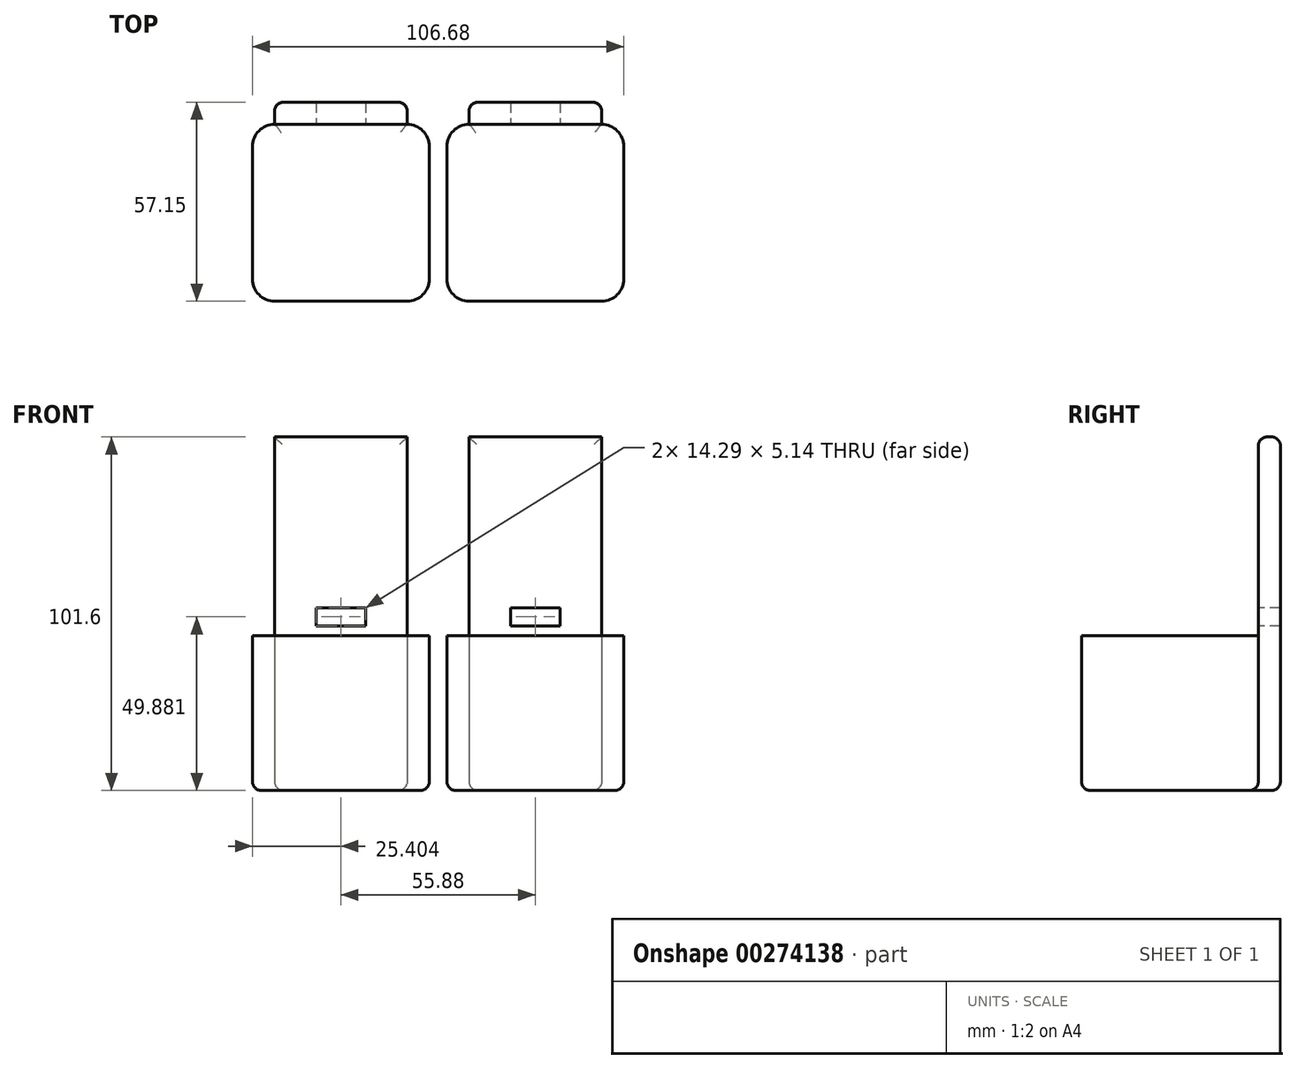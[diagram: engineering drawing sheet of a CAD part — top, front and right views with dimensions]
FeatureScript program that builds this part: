
annotation { "Feature Type Name" : "Feature", "Feature Type Description" : "" }
export const myFeature = defineFeature(function(context is Context, id is Id, definition is map)
    precondition{}
    {
        {
            var Q0;
            Q0=qCreatedBy(makeId("Top.planeOp"),FACE);
            var sketch = newSketch(context, id + "F0", { "sketchPlane" : qUnion([Q0])});
            skLineSegment(sketch, "E0.bottom", {"start": v(-13.8, 18.6) * mm, "end": v(24.3, 18.6) * mm});
            skLineSegment(sketch, "E0.top", {"start": v(-13.8, -32.2) * mm, "end": v(24.3, -32.2) * mm});
            skLineSegment(sketch, "E0.left", {"start": v(-20.15, 12.26) * mm, "end": v(-20.15, -25.84) * mm});
            skLineSegment(sketch, "E0.right", {"start": v(30.65, 12.26) * mm, "end": v(30.65, -25.84) * mm});
            skPoint(sketch, "E1.visualSharp", {"position": v(-20.15, 18.6) * mm});
            skArc(sketch, "E1.filletArc", {"start": v(-13.8, 18.6) * mm, "mid": v(-18.29, 16.75) * mm, "end": v(-20.15, 12.26) * mm});
            skPoint(sketch, "E2.visualSharp", {"position": v(30.65, 18.6) * mm});
            skArc(sketch, "E2.filletArc", {"start": v(30.65, 12.26) * mm, "mid": v(28.8, 16.75) * mm, "end": v(24.3, 18.6) * mm});
            skPoint(sketch, "E3.visualSharp", {"position": v(30.65, -32.2) * mm});
            skArc(sketch, "E3.filletArc", {"start": v(24.3, -32.2) * mm, "mid": v(28.8, -30.33) * mm, "end": v(30.65, -25.84) * mm});
            skPoint(sketch, "E4.visualSharp", {"position": v(-20.15, -32.2) * mm});
            skArc(sketch, "E4.filletArc", {"start": v(-20.15, -25.84) * mm, "mid": v(-18.29, -30.33) * mm, "end": v(-13.8, -32.2) * mm});
            skSolve(sketch);
        }
        {
            var Q0;
            Q0 = qSketchRegion(id + "F0", true);
            var Q1;
            Q1 = qSketchRegion(id + "F2", true);
            extrude(context, id + "F1", {"entities" : qUnion([Q0, Q1]), "depth" : 44.45 * mm});
        }
        {
            var Q0;
            Q0=makeQuery(id+"F1.opExtrude","SWEPT_FACE",FACE,{"disambiguationData":[OSD([sQuery(id+"F0.wireOp",EDGE,"E0.bottom")])]});
            var sketch = newSketch(context, id + "F2", { "sketchPlane" : qUnion([Q0])});
            skLineSegment(sketch, "E5.bottom", {"start": v(-24.3, 0) * mm, "end": v(13.8, 0) * mm});
            skLineSegment(sketch, "E5.top", {"start": v(-24.3, 101.6) * mm, "end": v(13.8, 101.6) * mm});
            skLineSegment(sketch, "E5.left", {"start": v(-24.3, 0) * mm, "end": v(-24.3, 101.6) * mm});
            skLineSegment(sketch, "E5.right", {"start": v(13.8, 0) * mm, "end": v(13.8, 101.6) * mm});
            skLineSegment(sketch, "E6.bottom", {"start": v(-12.4, 47.31) * mm, "end": v(1.89, 47.31) * mm});
            skLineSegment(sketch, "E6.top", {"start": v(-12.4, 52.45) * mm, "end": v(1.89, 52.45) * mm});
            skLineSegment(sketch, "E6.left", {"start": v(-12.4, 47.31) * mm, "end": v(-12.4, 52.45) * mm});
            skLineSegment(sketch, "E6.right", {"start": v(1.89, 47.31) * mm, "end": v(1.89, 52.45) * mm});
            skSolve(sketch);
        }
        {
            var Q0;
            {var subQ0=sQuery(id+"F2.wireOp",EDGE,"E5.bottom");Q0=makeQuery(id+"F2.imprint","IMPRINT",FACE,{"disambiguationData":[TD([[makeQuery(id+"F2.imprint","IMPRINT",EDGE,{"derivedFrom":subQ0}),-1.0]])]});}
            var Q1;
            {var subQ2=sQuery(id+"F2.wireOp",EDGE,"E5.top");Q1=makeQuery(id+"F2.imprint","IMPRINT",FACE,{"disambiguationData":[TD([[makeQuery(id+"F2.imprint","IMPRINT",EDGE,{"derivedFrom":subQ2}),-1.0]])]});}
            extrude(context, id + "F3", {"entities" : qUnion([Q0, Q1]), "operationType" : NewBodyOperationType.ADD, "depth" : 6.35 * mm});
        }
        {
            var Q0;
            Q0=makeQuery(id+"F1.opExtrude","SWEPT_BODY",BODY,{"disambiguationData":[OSD([sQuery(id+"F0.wireOp",EDGE,"E0.bottom"),sQuery(id+"F0.wireOp",EDGE,"E0.top"),sQuery(id+"F0.wireOp",EDGE,"E0.left"),sQuery(id+"F0.wireOp",EDGE,"E0.right"),sQuery(id+"F0.wireOp",EDGE,"E1.filletArc"),sQuery(id+"F0.wireOp",EDGE,"E2.filletArc"),sQuery(id+"F0.wireOp",EDGE,"E3.filletArc"),sQuery(id+"F0.wireOp",EDGE,"E4.filletArc")])]});
            transform(context, id + "F4", {"entities" : qUnion([Q0]), "transformType" : TransformType.TRANSLATION_3D, "dx" : 55.88 * mm, "dy" : 0 * mm, "dz" : 0 * mm, "makeCopy" : true});
        }
        {
            var Q0;
            Q0=makeQuery(id+"F4.opPattern","COPY",EDGE,{"derivedFrom":makeQuery(id+"F3.opExtrude","CAP_EDGE",EDGE,{"disambiguationData":[OSD([sQuery(id+"F2.wireOp",EDGE,"E5.left")])],"isStart":false}),"instanceName":"1"});
            var Q1;
            Q1=makeQuery(id+"F3.opExtrude","CAP_EDGE",EDGE,{"disambiguationData":[OSD([sQuery(id+"F2.wireOp",EDGE,"E5.left")])],"isStart":false});
            var Q2;
            Q2=makeQuery(id+"F3.opExtrude","CAP_EDGE",EDGE,{"disambiguationData":[OSD([sQuery(id+"F2.wireOp",EDGE,"E5.right")])],"isStart":false});
            var Q3;
            Q3=makeQuery(id+"F4.opPattern","COPY",EDGE,{"derivedFrom":makeQuery(id+"F3.opExtrude","CAP_EDGE",EDGE,{"disambiguationData":[OSD([sQuery(id+"F2.wireOp",EDGE,"E5.right")])],"isStart":false}),"instanceName":"1"});
            var Q4;
            Q4=makeQuery(id+"F3.opExtrude","CAP_EDGE",EDGE,{"disambiguationData":[OSD([sQuery(id+"F2.wireOp",EDGE,"E5.top")])],"isStart":false});
            var Q5;
            Q5=makeQuery(id+"F4.opPattern","COPY",EDGE,{"derivedFrom":makeQuery(id+"F3.opExtrude","CAP_EDGE",EDGE,{"disambiguationData":[OSD([sQuery(id+"F2.wireOp",EDGE,"E5.top")])],"isStart":false}),"instanceName":"1"});
            var Q6;
            Q6=makeQuery(id+"F4.opPattern","COPY",EDGE,{"derivedFrom":makeQuery(id+"F3.opExtrude","CAP_EDGE",EDGE,{"disambiguationData":[OSD([sQuery(id+"F2.wireOp",EDGE,"E5.top")])],"isStart":true}),"instanceName":"1"});
            var Q7;
            Q7=makeQuery(id+"F3.opExtrude","CAP_EDGE",EDGE,{"disambiguationData":[OSD([sQuery(id+"F2.wireOp",EDGE,"E5.top")])],"isStart":true});
            fillet(context, id + "F5", {"entities" : qUnion([Q0, Q1, Q2, Q3, Q4, Q5, Q6, Q7]), "radius" : 2.54 * mm, "tangentPropagation" : true, "allowEdgeOverflow" : false});
        }
        {
            var Q0;
            Q0=makeQuery(id+"F3.boolean.opBoolean","MERGE",FACE,{"derivedFrom":[makeQuery(id+"F1.opExtrude","CAP_FACE",FACE,{"disambiguationData":[OSD([sQuery(id+"F0.wireOp",EDGE,"E0.bottom"),sQuery(id+"F0.wireOp",EDGE,"E0.top"),sQuery(id+"F0.wireOp",EDGE,"E0.left"),sQuery(id+"F0.wireOp",EDGE,"E0.right"),sQuery(id+"F0.wireOp",EDGE,"E1.filletArc"),sQuery(id+"F0.wireOp",EDGE,"E2.filletArc"),sQuery(id+"F0.wireOp",EDGE,"E3.filletArc"),sQuery(id+"F0.wireOp",EDGE,"E4.filletArc")])],"isStart":true}),makeQuery(id+"F3.opExtrude","SWEPT_FACE",FACE,{"disambiguationData":[OSD([sQuery(id+"F2.wireOp",EDGE,"E5.bottom")])]})]});
            var Q1;
            Q1=makeQuery(id+"F4.opPattern","COPY",FACE,{"derivedFrom":makeQuery(id+"F3.boolean.opBoolean","MERGE",FACE,{"derivedFrom":[makeQuery(id+"F1.opExtrude","CAP_FACE",FACE,{"disambiguationData":[OSD([sQuery(id+"F0.wireOp",EDGE,"E0.bottom"),sQuery(id+"F0.wireOp",EDGE,"E0.top"),sQuery(id+"F0.wireOp",EDGE,"E0.left"),sQuery(id+"F0.wireOp",EDGE,"E0.right"),sQuery(id+"F0.wireOp",EDGE,"E1.filletArc"),sQuery(id+"F0.wireOp",EDGE,"E2.filletArc"),sQuery(id+"F0.wireOp",EDGE,"E3.filletArc"),sQuery(id+"F0.wireOp",EDGE,"E4.filletArc")])],"isStart":true}),makeQuery(id+"F3.opExtrude","SWEPT_FACE",FACE,{"disambiguationData":[OSD([sQuery(id+"F2.wireOp",EDGE,"E5.bottom")])]})]}),"instanceName":"1"});
            fillet(context, id + "F6", {"entities" : qUnion([Q0, Q1]), "radius" : 2.54 * mm, "tangentPropagation" : true, "allowEdgeOverflow" : false});
        }
    });
